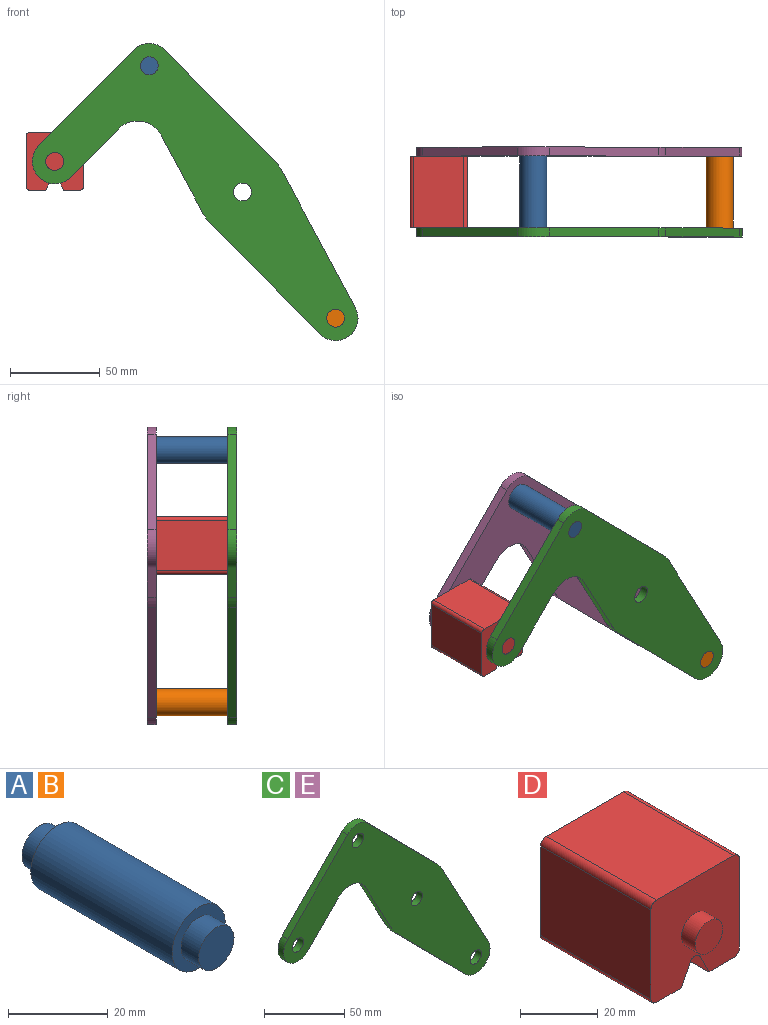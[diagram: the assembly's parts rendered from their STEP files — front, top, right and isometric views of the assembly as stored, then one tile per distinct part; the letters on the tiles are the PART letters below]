
ASSEMBLY  parts=5 mates=3
PART A: 7 faces, bbox 15x50x15 mm
  f0: cylinder r=7.5mm len=40mm, axis (0,-1,0), area 1885mm2, adj f2,f5
  f1: cylinder r=5mm len=10mm, axis (0,1,0), area 157.1mm2, adj f2,f3
  f2: plane 15x15mm, normal (0,-1,0), area 98.2mm2, adj f0,f1
  f3: plane 10x10mm, normal (0,-1,0), area 78.5mm2, adj f1
  f4: cylinder r=5mm len=10mm, axis (0,-1,0), area 157.1mm2, adj f5,f6
  f5: plane 15x15mm, normal (0,1,0), area 98.2mm2, adj f0,f4
  f6: plane 10x10mm, normal (0,1,0), area 78.5mm2, adj f4
PART B: same geometry as A
PART C: 18 faces, bbox 181.7x5x165.8 mm
  f0: plane 43.49x23.35mm, normal (-0.88,0,-0.47), area 246.8mm2, adj f1,f14,f16,f17
  f1: cylinder r=25mm len=5.75mm, axis (0,1,0), area 35.8mm2, adj f0,f2,f16,f17
  f2: plane 61.6x60.87mm, normal (-0.71,0,-0.7), area 433mm2, adj f1,f3,f16,f17
  f3: cylinder r=12.5mm len=21.39mm, axis (0,1,0), area 178.4mm2, adj f2,f4,f16,f17
  f4: plane 76.3x40.96mm, normal (0.88,0,0.47), area 433mm2, adj f3,f5,f16,f17
  f5: cylinder r=25mm len=5.75mm, axis (0,1,0), area 35.8mm2, adj f4,f6,f16,f17
  f6: plane 61.6x60.87mm, normal (0.71,0,0.7), area 433mm2, adj f5,f7,f16,f17
  f7: cylinder r=12.5mm len=17.78mm, axis (0,1,0), area 98.9mm2, adj f6,f8,f16,f17
  f8: plane 53.35x52.71mm, normal (-0.71,0,0.7), area 375mm2, adj f7,f9,f16,f17
  f9: cylinder r=12.5mm len=21.39mm, axis (0,1,0), area 196.3mm2, adj f8,f10,f16,f17
  f10: plane 26.86x26.54mm, normal (0.71,0,-0.7), area 188.8mm2, adj f9,f14,f16,f17
  f11: cylinder r=5mm len=10mm, axis (0,1,0), area 157.1mm2, adj f16,f17
  f12: cylinder r=5mm len=10mm, axis (0,1,0), area 157.1mm2, adj f16,f17
  f13: cylinder r=5mm len=10mm, axis (0,1,0), area 157.1mm2, adj f16,f17
  f14: cylinder r=15mm len=23.89mm, axis (0,1,0), area 140.2mm2, adj f0,f10,f16,f17
  f15: cylinder r=5mm len=10mm, axis (0,1,0), area 157.1mm2, adj f16,f17
  f16: plane 181.66x165.78mm, normal (0,-1,0), area 8710.1mm2, adj f0,f1,f2,f3,f4,f5,f6,f7
  f17: plane 181.66x165.78mm, normal (0,1,0), area 8710.1mm2, adj f0,f1,f2,f3,f4,f5,f6,f7
PART D: 18 faces, bbox 32.1x50x32.1 mm
  f0: plane 40x28.08mm, normal (1,0,0), area 1123.1mm2, adj f4,f10,f13,f14
  f1: plane 40x9.04mm, normal (0,0,-1), area 361.6mm2, adj f2,f4,f10,f14
  f2: plane 40x6.42mm, normal (-0.89,0,-0.45), area 287.2mm2, adj f1,f4,f10,f15
  f3: plane 40x6.42mm, normal (0.89,0,-0.45), area 287.2mm2, adj f4,f5,f10,f15
  f4: plane 32.08x32.08mm, normal (0,-1,0), area 900.6mm2, adj f0,f1,f2,f3,f5,f6,f7,f9
  f5: plane 40x9.04mm, normal (0,0,-1), area 361.6mm2, adj f3,f4,f10,f16
  f6: plane 40x28.08mm, normal (0,0,1), area 1123.1mm2, adj f4,f10,f13,f17
  f7: plane 40x28.08mm, normal (-1,0,0), area 1123.1mm2, adj f4,f10,f16,f17
  f8: plane 10x10mm, normal (0,-1,0), area 78.5mm2, adj f9
  f9: cylinder r=5mm len=10mm, axis (0,1,0), area 157.1mm2, adj f4,f8
  f10: plane 32.08x32.08mm, normal (0,1,0), area 900.6mm2, adj f0,f1,f2,f3,f5,f6,f7,f12
  f11: plane 10x10mm, normal (0,1,0), area 78.5mm2, adj f12
  f12: cylinder r=5mm len=10mm, axis (0,-1,0), area 157.1mm2, adj f10,f11
  f13: cylinder r=2mm len=40mm, axis (0,1,0), area 125.7mm2, adj f0,f4,f6,f10
  f14: cylinder r=2mm len=40mm, axis (0,-1,0), area 125.7mm2, adj f0,f1,f4,f10
  f15: cylinder r=2mm len=40mm, axis (0,1,0), area 177.1mm2, adj f2,f3,f4,f10
  f16: cylinder r=2mm len=40mm, axis (0,1,0), area 125.7mm2, adj f4,f5,f7,f10
  f17: cylinder r=2mm len=40mm, axis (0,-1,0), area 125.7mm2, adj f4,f6,f7,f10
PART E: same geometry as C
PLACE A t=(1.68,-69.66,-7.27)mm
PLACE B t=(105.63,-69.66,-148.05)mm
PLACE C t=(1.68,-69.66,-7.27)mm
PLACE D t=(1.68,-69.66,-7.27)mm
PLACE E t=(1.68,-24.66,-7.27)mm fixed
MATE fastened C.f7 <-> A.f0  axis (0,1,0) through (-50.29,-69.66,63.12)mm
MATE fastened B.f0 <-> C.f3  axis (0,1,0) through (53.66,-69.66,-77.66)mm
MATE revolute D.f9 <-> E.f9  axis (0,-1,0) through (-103.01,-29.66,9.77)mm
